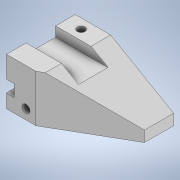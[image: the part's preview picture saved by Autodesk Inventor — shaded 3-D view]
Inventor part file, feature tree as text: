
AUTODESK INVENTOR PART (.ipt)
format: ipt  version: 2022.2 (Build 262287030, 287C)  size: 150,528 bytes
history: native  units: in
note: dims shown in document units (in); Inventor stores cm internally (conversion verified against a paired STEP export)
features: extrude x4, sketch x4, projected_geometry x1
ambient origin geometry x8: Origin, YZ Plane, XZ Plane, XY Plane, X Axis, Y Axis, Z Axis, Center Point
bodies: Solid1 (feature_tree)
feature tree (9):
  extrude  "Extrusion1"  Depth=4.7244in
  extrude  "Extrusion3"  Depth=2.9528in
  extrude  "Extrusion4"  Depth=0.9843in
  extrude  "Extrusion5"  Depth=3.5433in
  sketch  "Sketch1"  dims[d0=6.8898in d1=4.7244in]
  sketch  "Sketch4"  dims[d2=9.8425in d3=0.0in d6=2.9528in]
  sketch  "Sketch5"  dims[d7=1.9685in d8=0.9843in]
  projected_geometry  "Projected Loop1"
  sketch  "Sketch6"  dims[d9=0.0in d10=0.0in d11=3.5433in d12=30.0deg d13=0.7874in d14=1.9685in d15=1.378in d16=1.1811in d17=0.7874in d18=0.9843in d19=0.0in d20=0.0in d21=30.0deg d22=2.9528in d23=1.5748in d24=0.9843in d25=0.7874in d26=0.0in d27=0.0in]
